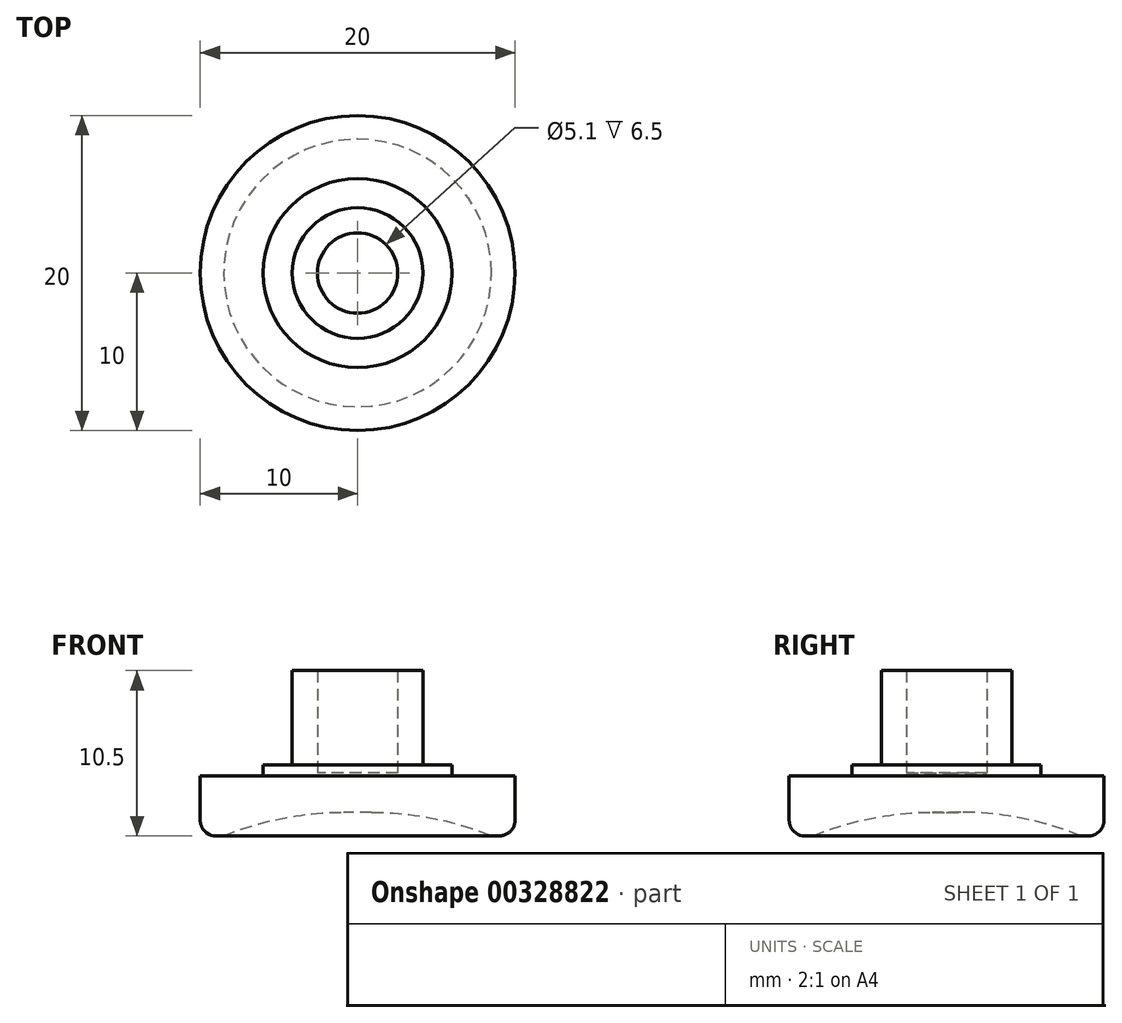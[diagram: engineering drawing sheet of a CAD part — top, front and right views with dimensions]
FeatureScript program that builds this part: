
annotation { "Feature Type Name" : "Feature", "Feature Type Description" : "" }
export const myFeature = defineFeature(function(context is Context, id is Id, definition is map)
    precondition{}
    {
        {
            var Q0;
            Q0=qCreatedBy(makeId("Top.planeOp"),FACE);
            var sketch = newSketch(context, id + "F0", { "sketchPlane" : qUnion([Q0])});
            skCircle(sketch, "E0", {"center": v(0, 0) * mm, "radius": 10 * mm});
            skCircle(sketch, "E1", {"center": v(0, 0) * mm, "radius": 4.15 * mm});
            skCircle(sketch, "E2", {"center": v(0, 0) * mm, "radius": 2.55 * mm});
            skCircle(sketch, "E3", {"center": v(0, 0) * mm, "radius": 6 * mm});
            skSolve(sketch);
        }
        {
            var Q0;
            Q0=makeQuery(id+"F0.imprint","IMPRINT",FACE,{"disambiguationData":[TD([[makeQuery(id+"F0.imprint","IMPRINT",EDGE,{"derivedFrom":sQuery(id+"F0.wireOp",EDGE,"ySUM5AKg-UsGA-TdMw-ahrU-znDptPXNU6Iv")}),1.0]])]});
            var Q1;
            Q1=makeQuery(id+"F0.imprint","IMPRINT",FACE,{"disambiguationData":[TD([[makeQuery(id+"F0.imprint","IMPRINT",EDGE,{"derivedFrom":sQuery(id+"F0.wireOp",EDGE,"3p2e0aJR-XqUT-eeAG-qWKK-FXu0mRQuosiw")}),1.0]])]});
            var Q2;
            Q2=makeQuery(id+"F0.imprint","IMPRINT",FACE,{"disambiguationData":[TD([[makeQuery(id+"F0.imprint","IMPRINT",EDGE,{"derivedFrom":sQuery(id+"F0.wireOp",EDGE,"E0")}),1.0]])]});
            var Q3;
            Q3=makeQuery(id+"F0.imprint","IMPRINT",FACE,{"disambiguationData":[TD([[makeQuery(id+"F0.imprint","IMPRINT",EDGE,{"derivedFrom":sQuery(id+"F0.wireOp",EDGE,"E2")}),1.0]])]});
            var Q4;
            Q4=makeQuery(id+"F0.imprint","IMPRINT",FACE,{"disambiguationData":[TD([[makeQuery(id+"F0.imprint","IMPRINT",EDGE,{"derivedFrom":sQuery(id+"F0.wireOp",EDGE,"E1")}),1.0]])]});
            extrude(context, id + "F1", {"entities" : qUnion([Q0, Q1, Q2, Q3, Q4]), "depth" : 4 * mm});
        }
        {
            var Q0;
            Q0=makeQuery(id+"F0.imprint","IMPRINT",FACE,{"disambiguationData":[TD([[makeQuery(id+"F0.imprint","IMPRINT",EDGE,{"derivedFrom":sQuery(id+"F0.wireOp",EDGE,"E1")}),1.0]])]});
            extrude(context, id + "F2", {"entities" : qUnion([Q0]), "operationType" : NewBodyOperationType.ADD, "depth" : 10.5 * mm});
        }
        {
            var Q0;
            Q0=makeQuery(id+"F0.imprint","IMPRINT",FACE,{"disambiguationData":[TD([[makeQuery(id+"F0.imprint","IMPRINT",EDGE,{"derivedFrom":sQuery(id+"F0.wireOp",EDGE,"E1")}),-1.0]])]});
            var Q1;
            Q1=makeQuery(id+"F0.imprint","IMPRINT",FACE,{"disambiguationData":[TD([[makeQuery(id+"F0.imprint","IMPRINT",EDGE,{"derivedFrom":sQuery(id+"F0.wireOp",EDGE,"3p2e0aJR-XqUT-eeAG-qWKK-FXu0mRQuosiw")}),-1.0]])]});
            extrude(context, id + "F3", {"entities" : qUnion([Q0, Q1]), "operationType" : NewBodyOperationType.ADD, "depth" : 4.5 * mm});
        }
        {
            var Q0;
            Q0=makeQuery(id+"F0.imprint","IMPRINT",FACE,{"disambiguationData":[TD([[makeQuery(id+"F0.imprint","IMPRINT",EDGE,{"derivedFrom":sQuery(id+"F0.wireOp",EDGE,"E0")}),1.0]])]});
            var sketch = newSketch(context, id + "F4", { "sketchPlane" : qUnion([Q0])});
            skCircle(sketch, "E4", {"center": v(0, 0) * mm, "radius": 8.5 * mm});
            skSolve(sketch);
        }
        {
            var Q0;
            Q0=makeQuery(id+"F4.imprint","IMPRINT",FACE,{"disambiguationData":[TD([[makeQuery(id+"F4.imprint","IMPRINT",EDGE,{"derivedFrom":sQuery(id+"F4.wireOp",EDGE,"E4")}),1.0]])]});
            var Q1;
            Q1=makeQuery(id+"F4.imprint","IMPRINT",FACE,{"disambiguationData":[TD([[makeQuery(id+"F4.imprint","IMPRINT",EDGE,{"derivedFrom":makeQuery(id+"F0.imprint","IMPRINT",EDGE,{"derivedFrom":sQuery(id+"F0.wireOp",EDGE,"E3")})}),1.0]])]});
            extrude(context, id + "F5", {"entities" : qUnion([Q0, Q1]), "operationType" : NewBodyOperationType.REMOVE, "depth" : 1.5 * mm});
        }
        {
            var Q0;
            Q0=makeQuery(id+"F5.boolean.opBoolean","COPY",FACE,{"derivedFrom":makeQuery(id+"F5.opExtrude","CAP_FACE",FACE,{"disambiguationData":[OSD([sQuery(id+"F4.wireOp",EDGE,"E4")])],"isStart":false})});
            fillet(context, id + "F6", {"entities" : qUnion([Q0]), "radius" : 20 * mm, "tangentPropagation" : true, "allowEdgeOverflow" : false});
        }
        {
            var Q0;
            Q0=makeQuery(id+"F1.opExtrude","CAP_EDGE",EDGE,{"disambiguationData":[OSD([sQuery(id+"F0.wireOp",EDGE,"E0")])],"isStart":true});
            fillet(context, id + "F7", {"entities" : qUnion([Q0]), "radius" : 1 * mm, "tangentPropagation" : true, "allowEdgeOverflow" : false});
        }
        {
            var Q0;
            Q0=makeQuery(id+"F1.opExtrude","CAP_FACE",FACE,{"disambiguationData":[OSD([sQuery(id+"F0.wireOp",EDGE,"E0"),sQuery(id+"F0.wireOp",EDGE,"E3")])],"isStart":false});
            extrude(context, id + "F8", {"entities" : qUnion([Q0]), "operationType" : NewBodyOperationType.REMOVE, "oppositeDirection" : true, "depth" : 0.2 * mm, "offsetDistance" : 25 * mm});
        }
    });
